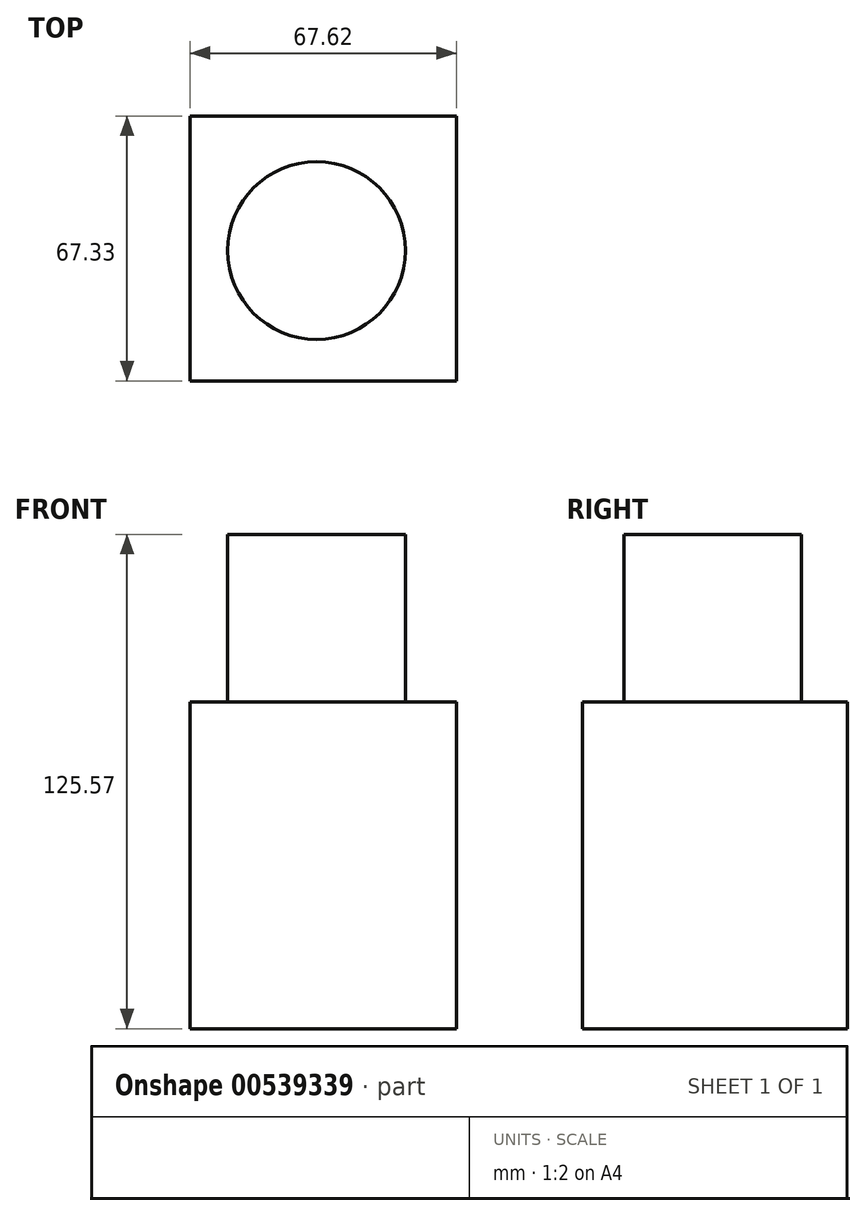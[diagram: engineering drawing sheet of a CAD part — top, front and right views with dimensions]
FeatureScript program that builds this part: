
annotation { "Feature Type Name" : "Feature", "Feature Type Description" : "" }
export const myFeature = defineFeature(function(context is Context, id is Id, definition is map)
    precondition{}
    {
        {
            var Q0;
            Q0=qCreatedBy(makeId("Top.planeOp"),FACE);
            var sketch = newSketch(context, id + "F0", { "sketchPlane" : qUnion([Q0])});
            skLineSegment(sketch, "E0.bottom", {"start": v(-32.12, 28.42) * mm, "end": v(35.5, 28.42) * mm});
            skLineSegment(sketch, "E0.top", {"start": v(-32.12, -38.9) * mm, "end": v(35.5, -38.9) * mm});
            skLineSegment(sketch, "E0.left", {"start": v(-32.12, 28.42) * mm, "end": v(-32.12, -38.9) * mm});
            skLineSegment(sketch, "E0.right", {"start": v(35.5, 28.42) * mm, "end": v(35.5, -38.9) * mm});
            skSolve(sketch);
        }
        {
            var Q0;
            Q0 = qSketchRegion(id + "F0", true);
            extrude(context, id + "F1", {"entities" : qUnion([Q0]), "depth" : 83.07 * mm, "offsetDistance" : 25.4 * mm});
        }
        {
            var Q0;
            Q0=makeQuery(id+"F1.opExtrude","CAP_FACE",FACE,{"disambiguationData":[OSD([sQuery(id+"F0.wireOp",EDGE,"E0.bottom"),sQuery(id+"F0.wireOp",EDGE,"E0.top"),sQuery(id+"F0.wireOp",EDGE,"E0.left"),sQuery(id+"F0.wireOp",EDGE,"E0.right")])],"isStart":false});
            var sketch = newSketch(context, id + "F2", { "sketchPlane" : qUnion([Q0])});
            skCircle(sketch, "E1", {"center": v(0, -5.78) * mm, "radius": 22.58 * mm});
            skSolve(sketch);
        }
        {
            var Q0;
            Q0 = qSketchRegion(id + "F2", true);
            extrude(context, id + "F3", {"entities" : qUnion([Q0]), "operationType" : NewBodyOperationType.ADD, "depth" : 42.5 * mm, "offsetDistance" : 25.4 * mm});
        }
    });
